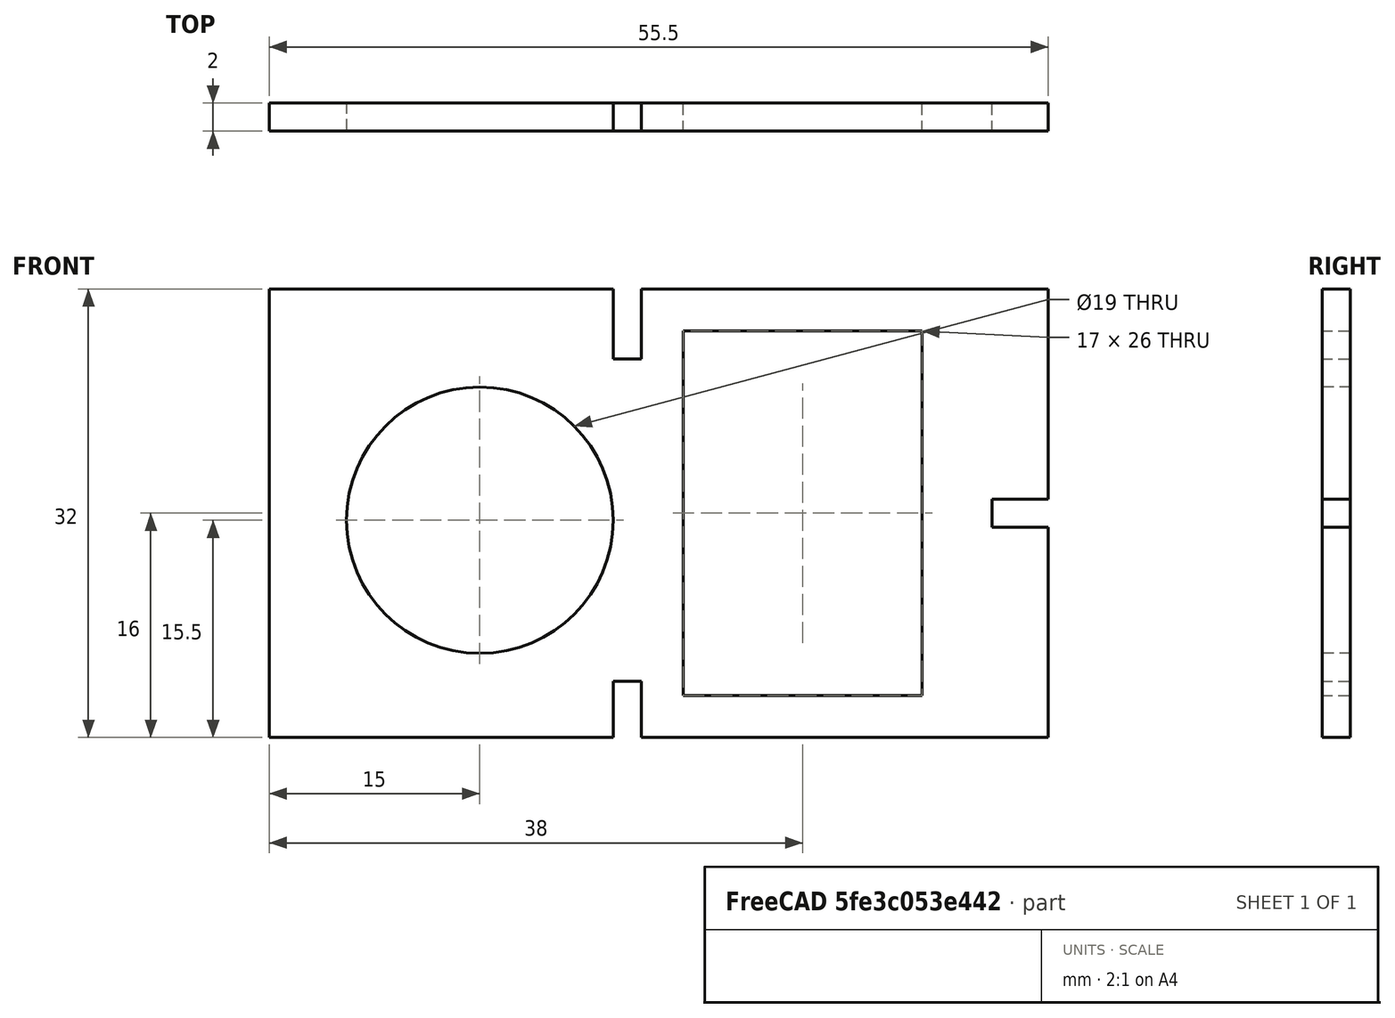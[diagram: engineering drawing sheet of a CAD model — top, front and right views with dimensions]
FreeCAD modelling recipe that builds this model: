
FCSTD DOCUMENT  (FreeCAD 0.14R3700 (Git))
Label: BIRR_fixMoteurAv
License: CC-BY 3.0
LicenseURL: http://creativecommons.org/licenses/by/3.0/
objects: Sketcher::SketchObject×1, Part::Extrusion×1, Part::Feature×1
note: 3 computed .brp shape members not serialized (recipe doc carries the construction recipe); baked Part::Feature solids carry a one-line shape summary decoded from their .brp

FEATURE [Sketcher::SketchObject] Sketch  label="fixMoteurAv"
  Placement = pos=(0,0,0) rot=(1,0,0;1.5708rad)
  sketch-geometry (21):
    g0: Circle CenterX=-12.75 CenterY=15.5 CenterZ=0 NormalX=0 NormalY=0 NormalZ=1 Radius=9.5
    g1: LineSegment StartX=1.75 StartY=29 StartZ=0 EndX=18.75 EndY=29 EndZ=0
    g2: LineSegment StartX=18.75 StartY=29 StartZ=0 EndX=18.75 EndY=3 EndZ=0
    g3: LineSegment StartX=18.75 StartY=3 StartZ=0 EndX=1.75 EndY=3 EndZ=0
    g4: LineSegment StartX=1.75 StartY=3 StartZ=0 EndX=1.75 EndY=29 EndZ=0
    g5: LineSegment StartX=-27.75 StartY=32 StartZ=0 EndX=-27.75 EndY=0 EndZ=0
    g6: LineSegment StartX=-27.75 StartY=32 StartZ=0 EndX=-3.25 EndY=32 EndZ=0
    g7: LineSegment StartX=-3.25 StartY=32 StartZ=0 EndX=-3.25 EndY=27 EndZ=0
    g8: LineSegment StartX=-3.25 StartY=27 StartZ=0 EndX=-1.25 EndY=27 EndZ=0
    g9: LineSegment StartX=-1.25 StartY=27 StartZ=0 EndX=-1.25 EndY=32 EndZ=0
    g10: LineSegment StartX=-1.25 StartY=32 StartZ=0 EndX=27.75 EndY=32 EndZ=0
    g11: LineSegment StartX=-27.75 StartY=0 StartZ=0 EndX=-3.25 EndY=0 EndZ=0
    g12: LineSegment StartX=-3.25 StartY=0 StartZ=0 EndX=-3.25 EndY=4 EndZ=0
    g13: LineSegment StartX=-3.25 StartY=4 StartZ=0 EndX=-1.25 EndY=4 EndZ=0
    g14: LineSegment StartX=-1.25 StartY=4 StartZ=0 EndX=-1.25 EndY=0 EndZ=0
    g15: LineSegment StartX=27.75 StartY=0 StartZ=0 EndX=-1.25 EndY=0 EndZ=0
    g16: LineSegment StartX=27.75 StartY=17 StartZ=0 EndX=23.75 EndY=17 EndZ=0
    g17: LineSegment StartX=23.75 StartY=17 StartZ=0 EndX=23.75 EndY=15 EndZ=0
    g18: LineSegment StartX=23.75 StartY=15 StartZ=0 EndX=27.75 EndY=15 EndZ=0
    g19: LineSegment StartX=27.75 StartY=32 StartZ=0 EndX=27.75 EndY=17 EndZ=0
    g20: LineSegment StartX=27.75 StartY=0 StartZ=0 EndX=27.75 EndY=15 EndZ=0
  constraints (62):
    c: Coincident(g1,g2)
    c: Coincident(g2,g3)
    c: Coincident(g3,g4)
    c: Coincident(g4,g1)
    c: Horizontal(g1)
    c: Horizontal(g3)
    c: Vertical(g2)
    c: Vertical(g4)
    c: Vertical(g5)
    c: PointOnObject(g5,g-1)
    c: Symmetric(g5,g15,g-2)
    c: DistanceY(g15,g2) = 3
    c: DistanceX(g3) = -17
    c: Radius(g0) = 9.5
    c: DistanceY(g2) = -26
    c: DistanceY(g1,g10) = 3
    c: DistanceY(g5,g0) = 15.5
    c: DistanceX(g0,g1) = 14.5
    c: DistanceX(g0,g5) = -15
    c: Coincident(g6,g5)
    c: Horizontal(g6)
    c: Coincident(g7,g6)
    c: Vertical(g7)
    c: Coincident(g8,g7)
    c: Horizontal(g8)
    c: Coincident(g9,g8)
    c: Vertical(g9)
    c: Coincident(g10,g9)
    c: Horizontal(g10)
    c: DistanceY(g7) = -5
    c: DistanceX(g6,g9) = 2
    c: Coincident(g11,g5)
    c: Horizontal(g11)
    c: Coincident(g12,g11)
    c: Vertical(g12)
    c: Coincident(g13,g12)
    c: Coincident(g14,g13)
    c: Vertical(g14)
    c: Coincident(g15,g14)
    c: Horizontal(g15)
    c: DistanceY(g12) = 4
    c: Horizontal(g13)
    c: Coincident(g16,g17)
    c: Coincident(g17,g18)
    c: Horizontal(g16)
    c: Horizontal(g18)
    c: Vertical(g17)
    c: Coincident(g19,g10)
    c: Coincident(g19,g16)
    c: Vertical(g19)
    c: Coincident(g20,g15)
    c: Coincident(g20,g18)
    c: Vertical(g20)
    c: DistanceX(g18) = 4
    c: PointOnObject(g6,g10)
    c: DistanceY(g17) = -2
    c: PointOnObject(g16,g20)
    c: Equal(g19,g20)
    c: DistanceX(g3,g13) = -3
    c: PointOnObject(g8,g14)
    c: DistanceX(g10,g5) = -55.5
    c: PointOnObject(g7,g12)
FEATURE [Part::Extrusion] Extrude001
  Base = -> Sketch
  Dir = (0,2,0)
  Solid = true
FEATURE [Part::Feature] Extrude001001  label="fixMoteurAv_copy"
  shape: bbox 55.5 x 2 x 32 mm, 23 faces (baked)
